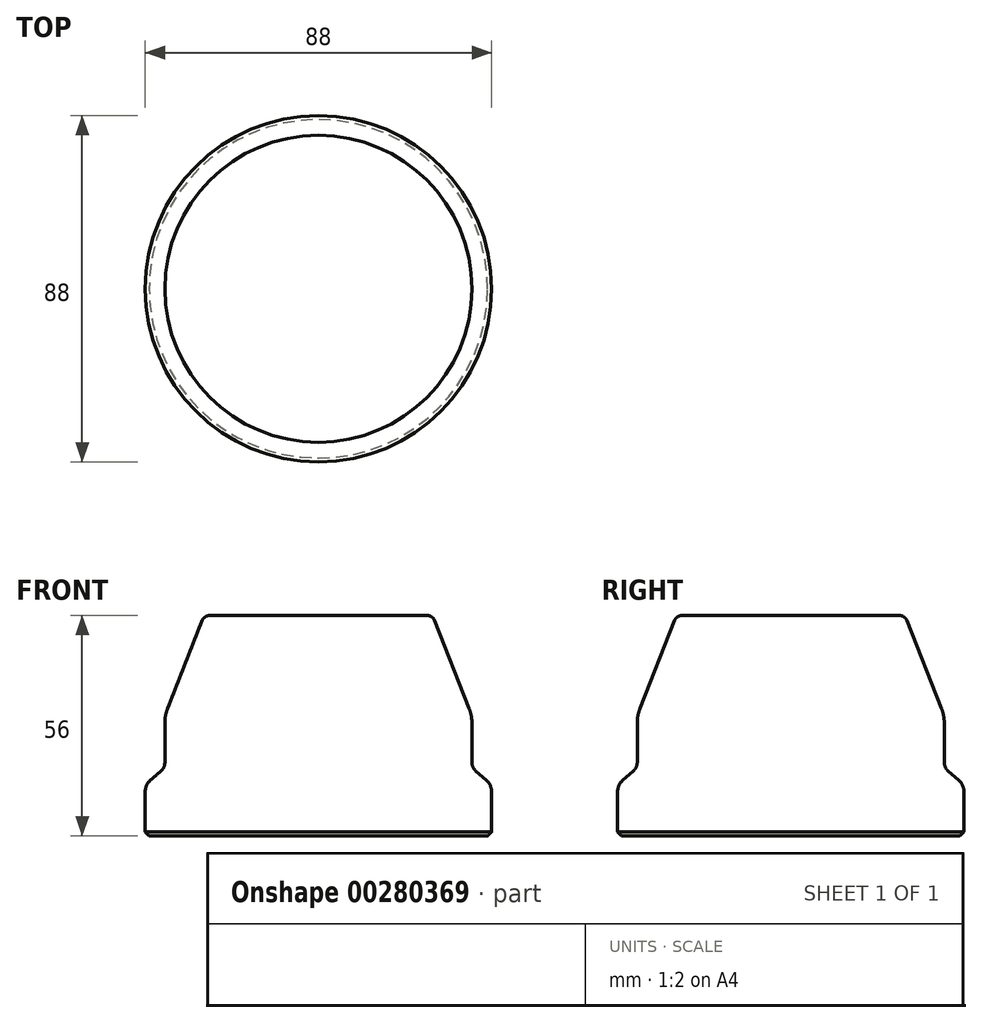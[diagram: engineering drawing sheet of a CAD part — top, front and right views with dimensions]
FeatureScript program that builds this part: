
annotation { "Feature Type Name" : "Feature", "Feature Type Description" : "" }
export const myFeature = defineFeature(function(context is Context, id is Id, definition is map)
    precondition{}
    {
        {
            var Q0;
            Q0=qCreatedBy(makeId("Front.planeOp"),FACE);
            var sketch = newSketch(context, id + "F0", { "sketchPlane" : qUnion([Q0])});
            skLineSegment(sketch, "E0", {"start": v(0, 0) * mm, "end": v(0, 56) * mm});
            skLineSegment(sketch, "E1", {"start": v(0, 56) * mm, "end": v(27.64, 56) * mm});
            skLineSegment(sketch, "E2", {"start": v(29.5, 54.73) * mm, "end": v(38.3, 32.37) * mm});
            skLineSegment(sketch, "E3", {"start": v(39, 28.7) * mm, "end": v(39, 18.7) * mm});
            skLineSegment(sketch, "E4", {"start": v(40.04, 16.44) * mm, "end": v(42.62, 14.2) * mm});
            skLineSegment(sketch, "E5", {"start": v(44, 11.17) * mm, "end": v(44, 0) * mm});
            skLineSegment(sketch, "E6", {"start": v(44, 0) * mm, "end": v(0, 0) * mm});
            skPoint(sketch, "E7.visualSharp", {"position": v(29, 56) * mm});
            skArc(sketch, "E7.filletArc", {"start": v(29.5, 54.73) * mm, "mid": v(28.76, 55.65) * mm, "end": v(27.64, 56) * mm});
            skPoint(sketch, "E8.visualSharp", {"position": v(39, 30.6) * mm});
            skArc(sketch, "E8.filletArc", {"start": v(39, 28.7) * mm, "mid": v(38.82, 30.57) * mm, "end": v(38.3, 32.37) * mm});
            skPoint(sketch, "E9.visualSharp", {"position": v(39, 17.33) * mm});
            skArc(sketch, "E9.filletArc", {"start": v(39, 18.7) * mm, "mid": v(39.27, 17.46) * mm, "end": v(40.04, 16.44) * mm});
            skPoint(sketch, "E10.visualSharp", {"position": v(44, 13) * mm});
            skArc(sketch, "E10.filletArc", {"start": v(44, 11.17) * mm, "mid": v(43.64, 12.83) * mm, "end": v(42.62, 14.2) * mm});
            skSolve(sketch);
        }
        {
            var Q0;
            Q0 = qSketchRegion(id + "F0", true);
            var Q1;
            Q1=sQuery(id+"F0.wireOp",EDGE,"E0");
            revolve(context, id + "F1", {"entities" : qUnion([Q0]), "axis" : qUnion([Q1]), "revolveType" : RevolveType.FULL});
        }
        {
            var Q0;
            Q0=makeQuery(id+"F1.opRevolve","SWEPT_EDGE",EDGE,{"disambiguationData":[OSD([sQuery(id+"F0.wireOp",EDGE,"E5"),sQuery(id+"F0.wireOp",EDGE,"E6")])]});
            chamfer(context, id + "F2", {"entities" : qUnion([Q0]), "width" : 1 * mm, "tangentPropagation" : true});
        }
    });
